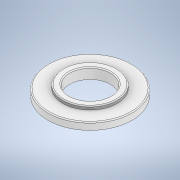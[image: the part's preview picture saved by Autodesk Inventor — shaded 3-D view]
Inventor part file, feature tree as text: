
AUTODESK INVENTOR PART (.ipt)
format: ipt  version: 2021 (Build 250183000, 183)  size: 136,192 bytes
history: native  units: mm
features: extrude x2, sketch x1, fillet x1
ambient origin geometry x8: Origin, YZ Plane, XZ Plane, XY Plane, X Axis, Y Axis, Z Axis, Center Point
bodies: Solid1 (feature_tree)
feature tree (4):
  sketch  "Sketch1"  dims[d0=17.5mm d1=11.3mm d2=8.5mm d3=2.2mm d4=0.0mm d5=1.5mm d6=0.0mm d7=0.2mm]
  extrude  "Extrusion1"  Depth=0.2mm
  extrude  "Extrusion2"  Depth=0.2mm
  fillet  "Fillet1"  Radius=2.2mm
